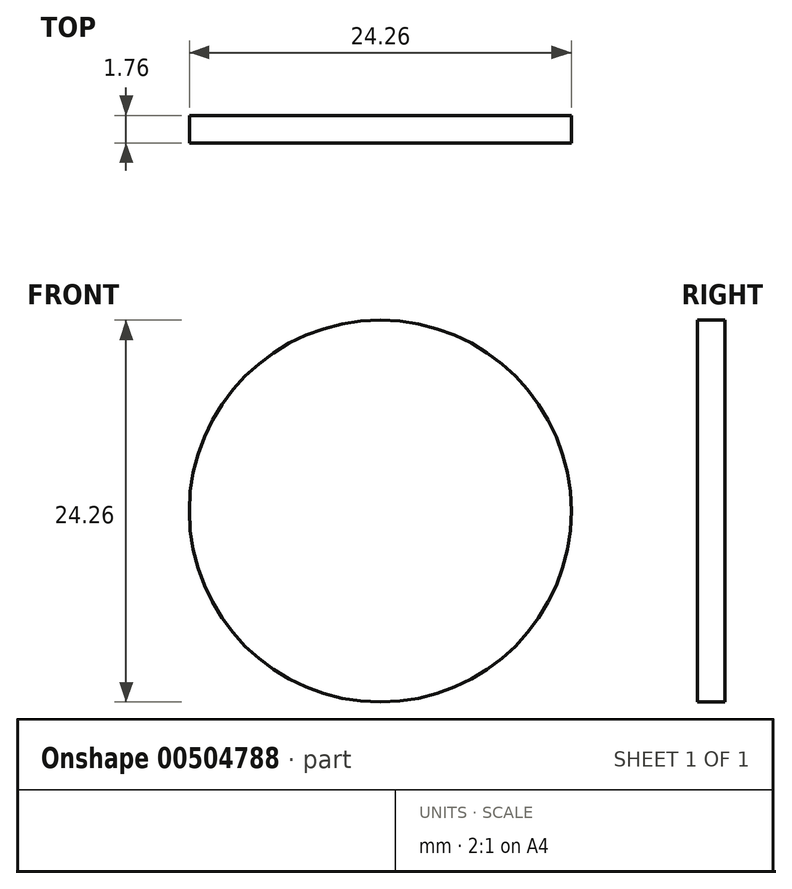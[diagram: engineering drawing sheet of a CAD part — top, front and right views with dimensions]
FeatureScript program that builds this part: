
annotation { "Feature Type Name" : "Feature", "Feature Type Description" : "" }
export const myFeature = defineFeature(function(context is Context, id is Id, definition is map)
    precondition{}
    {
        {
            var Q0;
            Q0=qCreatedBy(makeId("Front.planeOp"),FACE);
            var sketch = newSketch(context, id + "F0", { "sketchPlane" : qUnion([Q0])});
            skCircle(sketch, "E0", {"center": v(0, 0) * mm, "radius": 12.13 * mm});
            skSolve(sketch);
        }
        {
            var Q0;
            Q0=makeQuery(id+"F0.imprint","IMPRINT",FACE,{"disambiguationData":[TD([[makeQuery(id+"F0.imprint","IMPRINT",EDGE,{"derivedFrom":sQuery(id+"F0.wireOp",EDGE,"E0")}),1.0]])]});
            extrude(context, id + "F1", {"entities" : qUnion([Q0]), "endBound" : BoundingType.SYMMETRIC, "depth" : 1.75 * mm});
        }
    });
